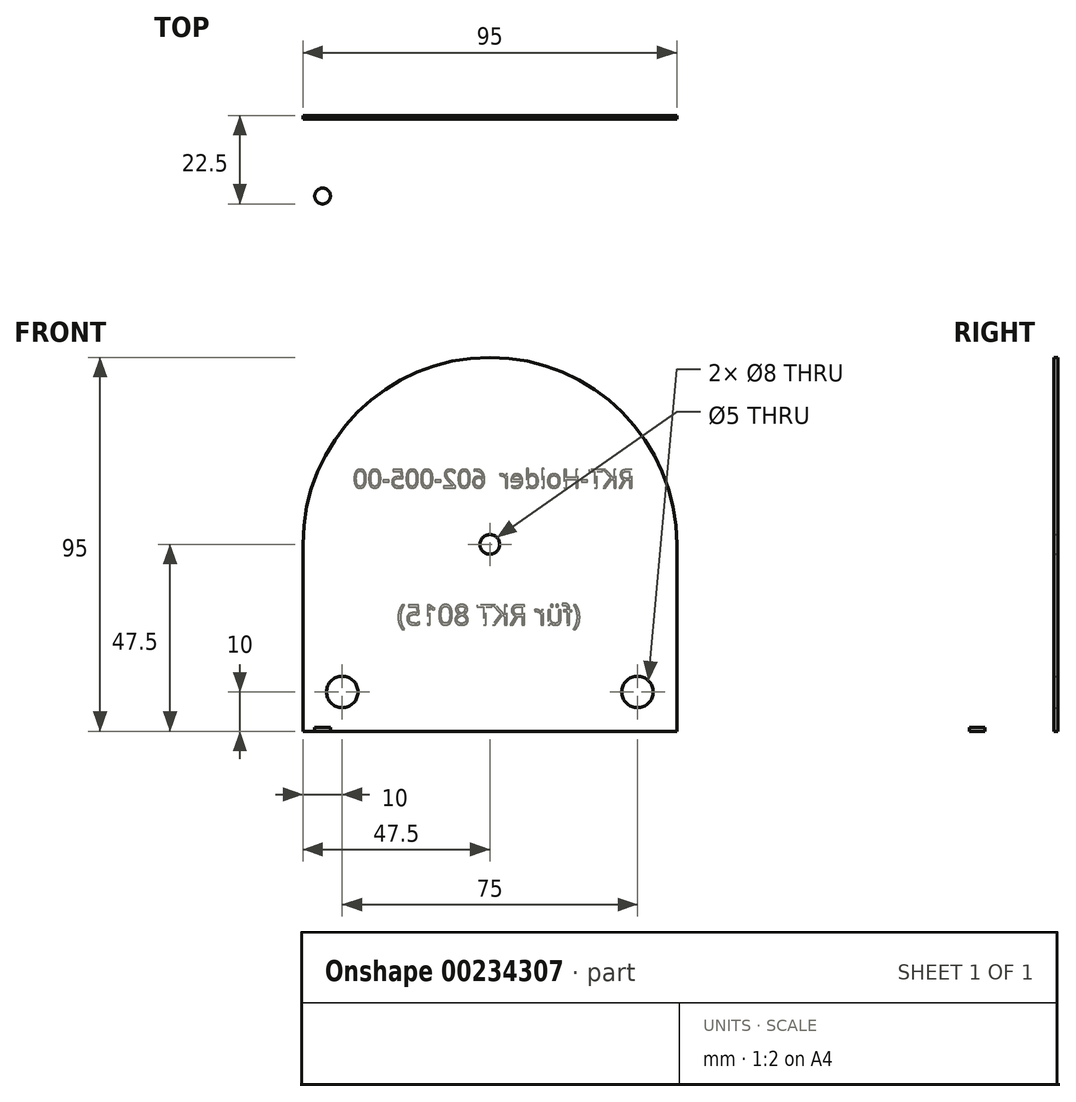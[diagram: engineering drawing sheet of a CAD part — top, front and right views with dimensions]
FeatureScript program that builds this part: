
annotation { "Feature Type Name" : "Feature", "Feature Type Description" : "" }
export const myFeature = defineFeature(function(context is Context, id is Id, definition is map)
    precondition{}
    {
        {
            var Q0;
            Q0=qCreatedBy(makeId("Front.planeOp"),FACE);
            var sketch = newSketch(context, id + "F0", { "sketchPlane" : qUnion([Q0])});
            skLineSegment(sketch, "E0.bottom", {"start": v(47.5, -47.5) * mm, "end": v(-47.5, -47.5) * mm});
            skLineSegment(sketch, "E0.top", {"start": v(0, 47.5) * mm, "end": v(0, 47.5) * mm});
            skLineSegment(sketch, "E0.left", {"start": v(47.5, -47.5) * mm, "end": v(47.5, 0) * mm});
            skLineSegment(sketch, "E0.right", {"start": v(-47.5, -47.5) * mm, "end": v(-47.5, 0) * mm});
            skPoint(sketch, "E0.middle", {"position": v(0, 0) * mm});
            skCircle(sketch, "E1", {"center": v(0, 0) * mm, "radius": 45 * mm, "construction": true});
            skCircle(sketch, "E2", {"center": v(0, 0) * mm, "radius": 2.5 * mm});
            skLineSegment(sketch, "E3", {"start": v(-47.5, -46.5) * mm, "end": v(47.5, -46.5) * mm});
            skCircle(sketch, "E4", {"center": v(-37.5, 37.5) * mm, "radius": 4 * mm});
            skCircle(sketch, "E5", {"center": v(37.5, 37.5) * mm, "radius": 4 * mm});
            skCircle(sketch, "E6", {"center": v(37.5, -37.5) * mm, "radius": 4 * mm});
            skCircle(sketch, "E7", {"center": v(-37.5, -37.5) * mm, "radius": 4 * mm});
            skPoint(sketch, "E8.visualSharp", {"position": v(47.5, 47.5) * mm});
            skArc(sketch, "E8.filletArc", {"start": v(47.5, 0) * mm, "mid": v(33.59, 33.59) * mm, "end": v(0, 47.5) * mm});
            skPoint(sketch, "E9.visualSharp", {"position": v(-47.5, 47.5) * mm});
            skArc(sketch, "E9.filletArc", {"start": v(0, 47.5) * mm, "mid": v(-33.59, 33.59) * mm, "end": v(-47.5, 0) * mm});
            skSolve(sketch);
        }
        {
            var Q0;
            Q0=makeQuery(id+"F0.imprint","IMPRINT",FACE,{"disambiguationData":[TD([[makeQuery(id+"F0.imprint","IMPRINT",EDGE,{"derivedFrom":sQuery(id+"F0.wireOp",EDGE,"E2")}),-1.0]])]});
            extrude(context, id + "F1", {"entities" : qUnion([Q0]), "depth" : 1 * mm, "offsetDistance" : 25 * mm});
        }
        {
            var Q0;
            {var subQ0=sQuery(id+"F0.wireOp",EDGE,"E0.bottom");Q0=makeQuery(id+"F0.imprint","IMPRINT",FACE,{"disambiguationData":[TD([[makeQuery(id+"F0.imprint","IMPRINT",EDGE,{"derivedFrom":subQ0}),-1.0]])]});}
            extrude(context, id + "F2", {"entities" : qUnion([Q0]), "operationType" : NewBodyOperationType.ADD, "depth" : 40 * mm, "offsetDistance" : 25 * mm});
        }
        {
            var Q0;
            Q0=makeQuery(id+"F2.opExtrude","SWEPT_FACE",FACE,{"disambiguationData":[OSD([sQuery(id+"F0.wireOp",EDGE,"E3")])]});
            var sketch = newSketch(context, id + "F3", { "sketchPlane" : qUnion([Q0])});
            skLineSegment(sketch, "E10", {"start": v(47.5, -20.5) * mm, "end": v(-47.5, -20.5) * mm, "construction": true});
            skCircle(sketch, "E11", {"center": v(42.5, -20.5) * mm, "radius": 2 * mm});
            skCircle(sketch, "E12.MirrorC", {"center": v(-42.5, -20.5) * mm, "radius": 2 * mm});
            skSolve(sketch);
        }
        {
            var Q0;
            Q0=makeQuery(id+"F3.imprint","IMPRINT",FACE,{"disambiguationData":[TD([[makeQuery(id+"F3.imprint","IMPRINT",EDGE,{"derivedFrom":sQuery(id+"F3.wireOp",EDGE,"E11")}),1.0]])]});
            var Q1;
            Q1=makeQuery(id+"F3.imprint","IMPRINT",FACE,{"disambiguationData":[TD([[makeQuery(id+"F3.imprint","IMPRINT",EDGE,{"derivedFrom":sQuery(id+"F3.wireOp",EDGE,"E12.MirrorC")}),-1.0]])]});
            extrude(context, id + "F4", {"entities" : qUnion([Q0, Q1]), "operationType" : NewBodyOperationType.REMOVE, "oppositeDirection" : true, "depth" : 25 * mm, "offsetDistance" : 25 * mm});
        }
        {
            var Q0;
            {var subQ0=sQuery(id+"F0.wireOp",EDGE,"E3");var subQ1=sQuery(id+"F0.wireOp",EDGE,"E0.right");var subQ2=sQuery(id+"F0.wireOp",EDGE,"E0.left");Q0=makeQuery(id+"F2.boolean.opBoolean","MERGE",FACE,{"derivedFrom":[makeQuery(id+"F1.opExtrude","CAP_FACE",FACE,{"disambiguationData":[OSD([sQuery(id+"F0.wireOp",EDGE,"E0.top"),subQ2,subQ1,sQuery(id+"F0.wireOp",EDGE,"E2"),subQ0,sQuery(id+"F0.wireOp",EDGE,"E4"),sQuery(id+"F0.wireOp",EDGE,"E5"),sQuery(id+"F0.wireOp",EDGE,"E6"),sQuery(id+"F0.wireOp",EDGE,"E7"),sQuery(id+"F0.wireOp",EDGE,"E8.filletArc"),sQuery(id+"F0.wireOp",EDGE,"E9.filletArc")])],"isStart":true}),makeQuery(id+"F2.opExtrude","CAP_FACE",FACE,{"disambiguationData":[OSD([sQuery(id+"F0.wireOp",EDGE,"E0.bottom"),subQ2,subQ1,subQ0])],"isStart":true})]});}
            var sketch = newSketch(context, id + "F5", { "sketchPlane" : qUnion([Q0])});
            skText(sketch, "E13", { "text": "RKT-Holder  602-005-00", "fontName": "OpenSans-Regular.ttf"});
            skText(sketch, "E14", { "text": "(für RKT 8015)", "fontName": "OpenSans-Regular.ttf"});
            const initialGuessF5  = {"E13": [-0.03669, 0.01437, 1, 0, 0.00467], "E14": [-0.02313, -0.02045, 1, 0, 0.00514]};
            skSetInitialGuess(sketch, initialGuessF5);
            skSolve(sketch);
        }
        {
            var Q0;
            Q0 = qSketchRegion(id + "F5", true);
            extrude(context, id + "F6", {"entities" : qUnion([Q0]), "operationType" : NewBodyOperationType.REMOVE, "oppositeDirection" : true, "depth" : .1 * mm, "offsetDistance" : 25 * mm});
        }
    });
